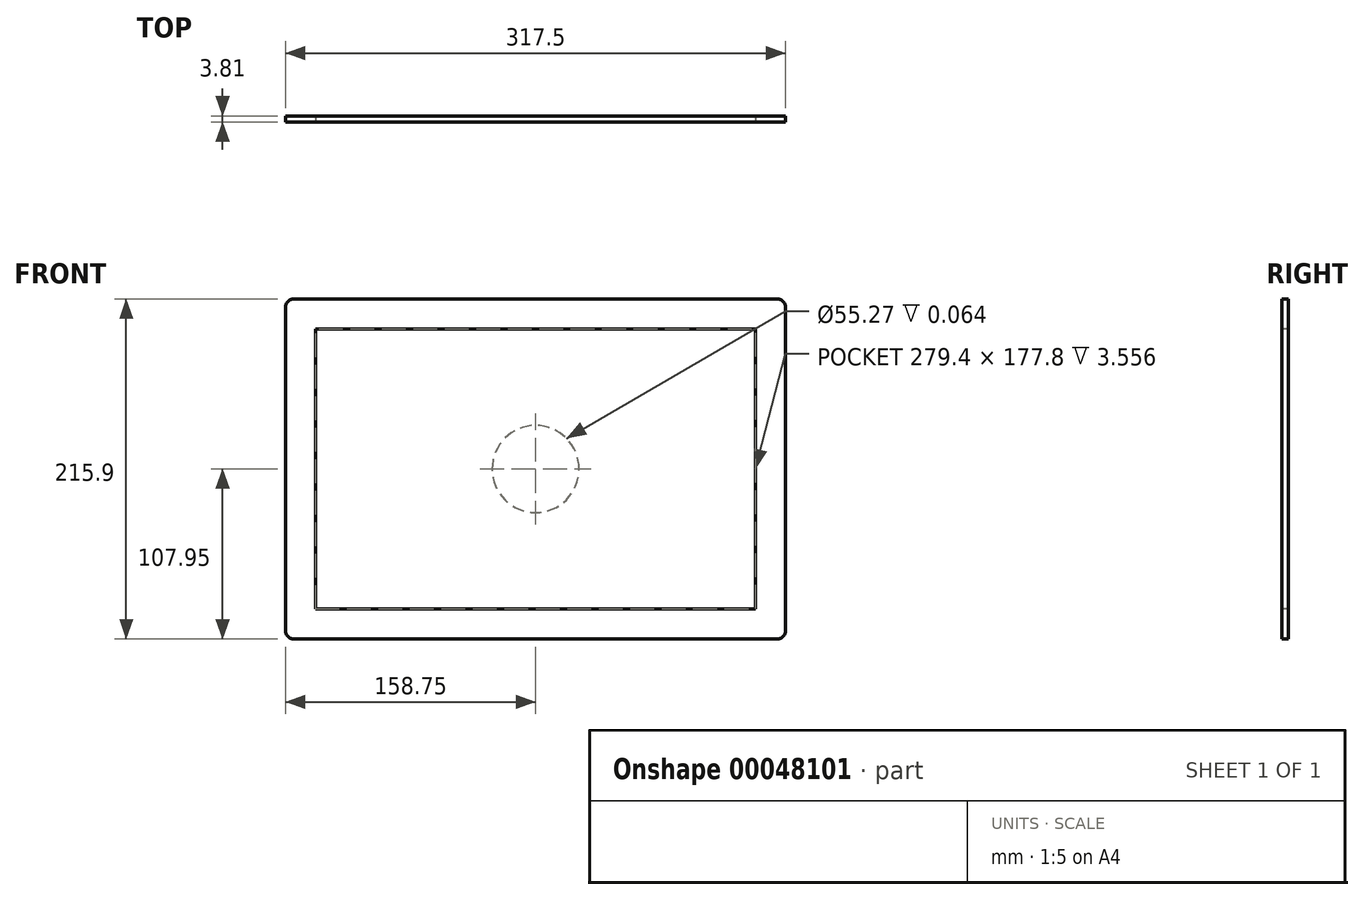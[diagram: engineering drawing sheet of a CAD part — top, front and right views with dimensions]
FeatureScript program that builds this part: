
annotation { "Feature Type Name" : "Feature", "Feature Type Description" : "" }
export const myFeature = defineFeature(function(context is Context, id is Id, definition is map)
    precondition{}
    {
        {
            var Q0;
            Q0=qCreatedBy(makeId("Front.planeOp"),FACE);
            var sketch = newSketch(context, id + "F0", { "sketchPlane" : qUnion([Q0])});
            skLineSegment(sketch, "E0.bottom", {"start": v(-158.75, 107.95) * mm, "end": v(158.75, 107.95) * mm});
            skLineSegment(sketch, "E0.top", {"start": v(-158.75, -107.95) * mm, "end": v(158.75, -107.95) * mm});
            skLineSegment(sketch, "E0.left", {"start": v(-158.75, 107.95) * mm, "end": v(-158.75, -107.95) * mm});
            skLineSegment(sketch, "E0.right", {"start": v(158.75, 107.95) * mm, "end": v(158.75, -107.95) * mm});
            skPoint(sketch, "E1", {"position": v(-2.39, 107.95) * mm});
            skPoint(sketch, "E2", {"position": v(-36.62, 0) * mm});
            skSolve(sketch);
        }
        {
            var Q0;
            Q0=makeQuery(id+"F0.imprint","IMPRINT",FACE,{"disambiguationData":[TD([[makeQuery(id+"F0.imprint","IMPRINT",EDGE,{"derivedFrom":sQuery(id+"F0.wireOp",EDGE,"E0.bottom")}),-1.0]])]});
            extrude(context, id + "F1", {"entities" : qUnion([Q0]), "depth" : 3.8 * mm});
        }
        {
            var Q0;
            Q0=makeQuery(id+"F1.opExtrude","SWEPT_EDGE",EDGE,{"disambiguationData":[OSD([sQuery(id+"F0.wireOp",EDGE,"E0.top"),sQuery(id+"F0.wireOp",EDGE,"E0.left")])]});
            fillet(context, id + "F2", {"entities" : qUnion([Q0]), "radius" : 5.08 * mm, "tangentPropagation" : true, "allowEdgeOverflow" : false});
        }
        {
            var Q0;
            Q0=makeQuery(id+"F1.opExtrude","SWEPT_EDGE",EDGE,{"disambiguationData":[OSD([sQuery(id+"F0.wireOp",EDGE,"E0.bottom"),sQuery(id+"F0.wireOp",EDGE,"E0.left")])]});
            var Q1;
            Q1=makeQuery(id+"F1.opExtrude","SWEPT_EDGE",EDGE,{"disambiguationData":[OSD([sQuery(id+"F0.wireOp",EDGE,"E0.bottom"),sQuery(id+"F0.wireOp",EDGE,"E0.right")])]});
            var Q2;
            Q2=makeQuery(id+"F1.opExtrude","SWEPT_EDGE",EDGE,{"disambiguationData":[OSD([sQuery(id+"F0.wireOp",EDGE,"E0.top"),sQuery(id+"F0.wireOp",EDGE,"E0.right")])]});
            fillet(context, id + "F3", {"entities" : qUnion([Q0, Q1, Q2]), "radius" : 5.08 * mm, "tangentPropagation" : true, "allowEdgeOverflow" : false});
        }
        {
            var Q0;
            Q0=makeQuery(id+"F1.opExtrude","CAP_FACE",FACE,{"disambiguationData":[OSD([sQuery(id+"F0.wireOp",EDGE,"E0.bottom"),sQuery(id+"F0.wireOp",EDGE,"E0.top"),sQuery(id+"F0.wireOp",EDGE,"E0.left"),sQuery(id+"F0.wireOp",EDGE,"E0.right")])],"isStart":false});
            var sketch = newSketch(context, id + "F4", { "sketchPlane" : qUnion([Q0])});
            skLineSegment(sketch, "E3.bottom", {"start": v(-139.7, 88.9) * mm, "end": v(139.7, 88.9) * mm});
            skLineSegment(sketch, "E3.top", {"start": v(-139.7, -88.9) * mm, "end": v(139.7, -88.9) * mm});
            skLineSegment(sketch, "E3.left", {"start": v(-139.7, 88.9) * mm, "end": v(-139.7, -88.9) * mm});
            skLineSegment(sketch, "E3.right", {"start": v(139.7, 88.9) * mm, "end": v(139.7, -88.9) * mm});
            skSolve(sketch);
        }
        {
            var Q0;
            Q0 = qSketchRegion(id + "F4", true);
            extrude(context, id + "F5", {"entities" : qUnion([Q0]), "operationType" : NewBodyOperationType.REMOVE, "oppositeDirection" : true, "depth" : 25.4 * mm});
        }
        {
            var Q0;
            Q0=makeQuery(id+"F0.imprint","IMPRINT",FACE,{"disambiguationData":[TD([[makeQuery(id+"F0.imprint","IMPRINT",EDGE,{"derivedFrom":sQuery(id+"F0.wireOp",EDGE,"E0.bottom")}),-1.0]])]});
            var sketch = newSketch(context, id + "F6", { "sketchPlane" : qUnion([Q0])});
            skLineSegment(sketch, "E4.bottom", {"start": v(-139.7, 88.9) * mm, "end": v(139.7, 88.9) * mm});
            skLineSegment(sketch, "E4.top", {"start": v(-139.7, -88.9) * mm, "end": v(139.7, -88.9) * mm});
            skLineSegment(sketch, "E4.left", {"start": v(-139.7, 88.9) * mm, "end": v(-139.7, -88.9) * mm});
            skLineSegment(sketch, "E4.right", {"start": v(139.7, 88.9) * mm, "end": v(139.7, -88.9) * mm});
            skSolve(sketch);
        }
        {
            var Q0;
            Q0 = qSketchRegion(id + "F6", true);
            extrude(context, id + "F7", {"entities" : qUnion([Q0]), "operationType" : NewBodyOperationType.ADD, "depth" : 0.25 * mm});
        }
        {
            var Q0;
            Q0=makeQuery(id+"F0.imprint","IMPRINT",FACE,{"disambiguationData":[TD([[makeQuery(id+"F0.imprint","IMPRINT",EDGE,{"derivedFrom":sQuery(id+"F0.wireOp",EDGE,"E0.bottom")}),-1.0]])]});
            var sketch = newSketch(context, id + "F8", { "sketchPlane" : qUnion([Q0])});
            skCircle(sketch, "E5", {"center": v(0, 0) * mm, "radius": 27.64 * mm});
            skSolve(sketch);
        }
        {
            var Q0;
            Q0 = qSketchRegion(id + "F8", true);
            extrude(context, id + "F9", {"entities" : qUnion([Q0]), "operationType" : NewBodyOperationType.REMOVE, "endBound" : BoundingType.SYMMETRIC, "oppositeDirection" : true, "depth" : 0.13 * mm});
        }
    });
